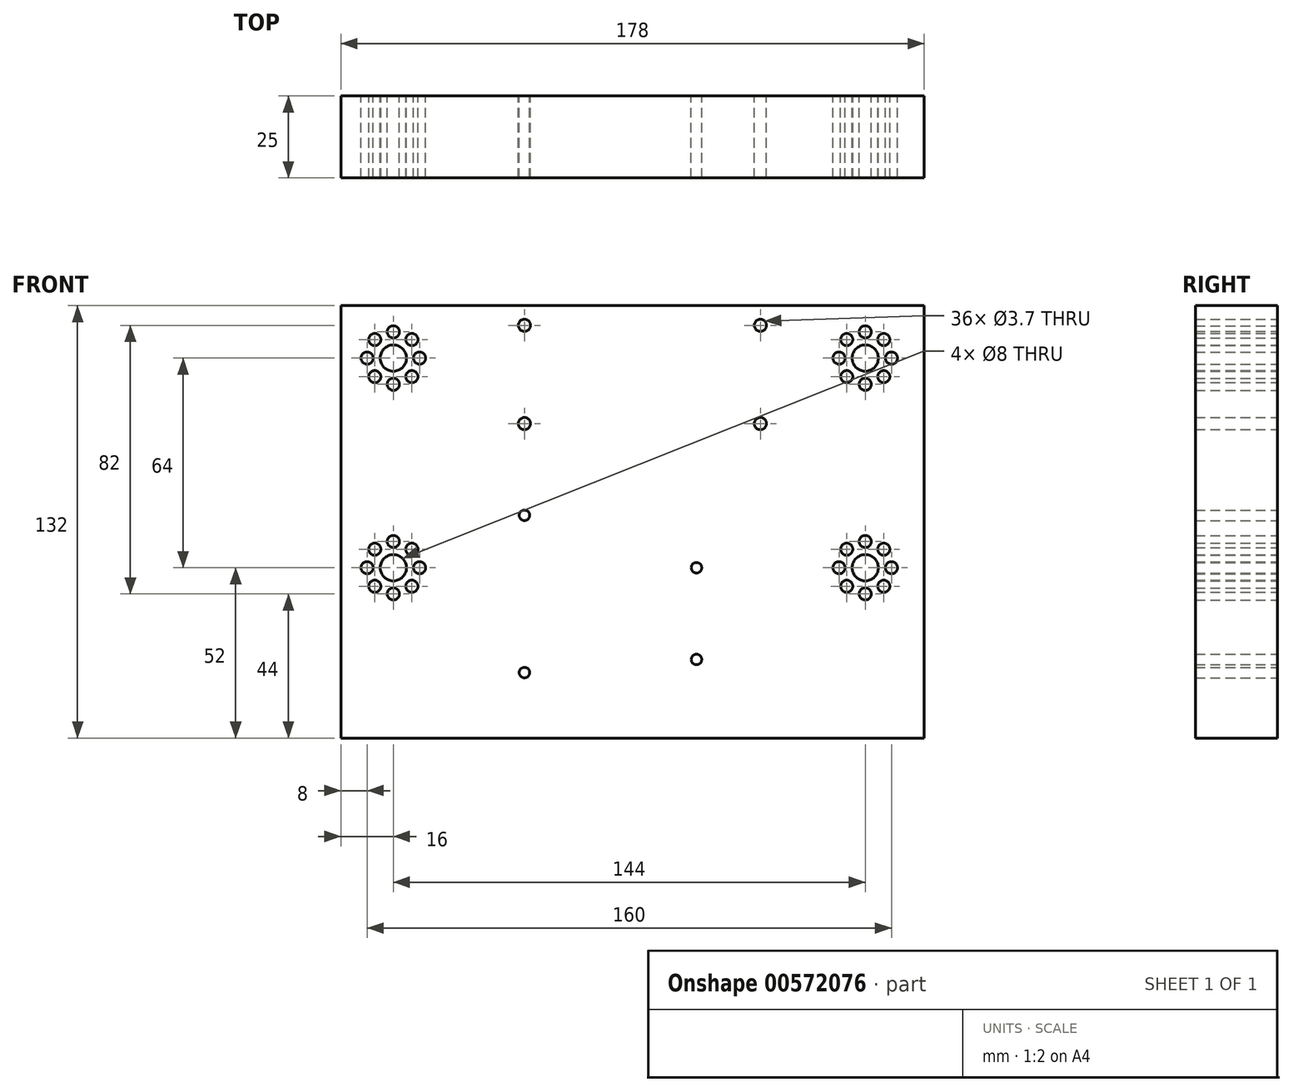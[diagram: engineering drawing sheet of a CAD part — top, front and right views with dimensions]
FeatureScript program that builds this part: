
annotation { "Feature Type Name" : "Feature", "Feature Type Description" : "" }
export const myFeature = defineFeature(function(context is Context, id is Id, definition is map)
    precondition{}
    {
        {
            var Q0;
            Q0=qCreatedBy(makeId("Front.planeOp"),FACE);
            var sketch = newSketch(context, id + "F0", { "sketchPlane" : qUnion([Q0])});
            skLineSegment(sketch, "E0.bottom", {"start": v(-89, 0) * mm, "end": v(89, 0) * mm});
            skLineSegment(sketch, "E0.top", {"start": v(-89, -132) * mm, "end": v(89, -132) * mm});
            skLineSegment(sketch, "E0.left", {"start": v(-89, 0) * mm, "end": v(-89, -132) * mm});
            skLineSegment(sketch, "E0.right", {"start": v(89, 0) * mm, "end": v(89, -132) * mm});
            skCircle(sketch, "E1", {"center": v(-73, -16) * mm, "radius": 4 * mm});
            skCircle(sketch, "E2", {"center": v(-73, -24) * mm, "radius": 1.85 * mm});
            skCircle(sketch, "E3.1.0", {"center": v(-67.34, -21.66) * mm, "radius": 1.85 * mm});
            skCircle(sketch, "E3.2.0", {"center": v(-65, -16) * mm, "radius": 1.85 * mm});
            skCircle(sketch, "E3.3.0", {"center": v(-67.34, -10.34) * mm, "radius": 1.85 * mm});
            skCircle(sketch, "E3.4.0", {"center": v(-73, -8) * mm, "radius": 1.85 * mm});
            skCircle(sketch, "E3.5.0", {"center": v(-78.66, -10.34) * mm, "radius": 1.85 * mm});
            skCircle(sketch, "E3.6.0", {"center": v(-81, -16) * mm, "radius": 1.85 * mm});
            skCircle(sketch, "E3.7.0", {"center": v(-78.66, -21.66) * mm, "radius": 1.85 * mm});
            skCircle(sketch, "E4.0.1.0", {"center": v(-73, -80) * mm, "radius": 4 * mm});
            skPoint(sketch, "E4.0.1.1", {"position": v(-73, -80) * mm});
            skCircle(sketch, "E4.0.1.2", {"center": v(-73, -88) * mm, "radius": 1.85 * mm});
            skCircle(sketch, "E4.0.1.3", {"center": v(-67.34, -85.66) * mm, "radius": 1.85 * mm});
            skCircle(sketch, "E4.0.1.4", {"center": v(-65, -80) * mm, "radius": 1.85 * mm});
            skCircle(sketch, "E4.0.1.5", {"center": v(-67.34, -74.34) * mm, "radius": 1.85 * mm});
            skCircle(sketch, "E4.0.1.6", {"center": v(-78.66, -74.34) * mm, "radius": 1.85 * mm});
            skCircle(sketch, "E4.0.1.7", {"center": v(-73, -72) * mm, "radius": 1.85 * mm});
            skCircle(sketch, "E4.0.1.8", {"center": v(-81, -80) * mm, "radius": 1.85 * mm});
            skCircle(sketch, "E4.0.1.9", {"center": v(-78.66, -85.66) * mm, "radius": 1.85 * mm});
            skCircle(sketch, "E4.1.0.0", {"center": v(71, -16) * mm, "radius": 4 * mm});
            skPoint(sketch, "E4.1.0.1", {"position": v(71, -16) * mm});
            skCircle(sketch, "E4.1.0.2", {"center": v(71, -24) * mm, "radius": 1.85 * mm});
            skCircle(sketch, "E4.1.0.3", {"center": v(76.66, -21.66) * mm, "radius": 1.85 * mm});
            skCircle(sketch, "E4.1.0.4", {"center": v(79, -16) * mm, "radius": 1.85 * mm});
            skCircle(sketch, "E4.1.0.5", {"center": v(76.66, -10.34) * mm, "radius": 1.85 * mm});
            skCircle(sketch, "E4.1.0.6", {"center": v(65.34, -10.34) * mm, "radius": 1.85 * mm});
            skCircle(sketch, "E4.1.0.7", {"center": v(71, -8) * mm, "radius": 1.85 * mm});
            skCircle(sketch, "E4.1.0.8", {"center": v(63, -16) * mm, "radius": 1.85 * mm});
            skCircle(sketch, "E4.1.0.9", {"center": v(65.34, -21.66) * mm, "radius": 1.85 * mm});
            skCircle(sketch, "E4.1.1.0", {"center": v(71, -80) * mm, "radius": 4 * mm});
            skPoint(sketch, "E4.1.1.1", {"position": v(71, -80) * mm});
            skCircle(sketch, "E4.1.1.2", {"center": v(71, -88) * mm, "radius": 1.85 * mm});
            skCircle(sketch, "E4.1.1.3", {"center": v(76.66, -85.66) * mm, "radius": 1.85 * mm});
            skCircle(sketch, "E4.1.1.4", {"center": v(79, -80) * mm, "radius": 1.85 * mm});
            skCircle(sketch, "E4.1.1.5", {"center": v(76.66, -74.34) * mm, "radius": 1.85 * mm});
            skCircle(sketch, "E4.1.1.6", {"center": v(65.34, -74.34) * mm, "radius": 1.85 * mm});
            skCircle(sketch, "E4.1.1.7", {"center": v(71, -72) * mm, "radius": 1.85 * mm});
            skCircle(sketch, "E4.1.1.8", {"center": v(63, -80) * mm, "radius": 1.85 * mm});
            skCircle(sketch, "E4.1.1.9", {"center": v(65.34, -85.66) * mm, "radius": 1.85 * mm});
            skLineSegment(sketch, "E4.direction1", {"start": v(-78.66, -21.66) * mm, "end": v(65.34, -21.66) * mm, "construction": true});
            skLineSegment(sketch, "E4.direction2", {"start": v(-78.66, -21.66) * mm, "end": v(-78.66, -85.66) * mm, "construction": true});
            skCircle(sketch, "E5", {"center": v(-33, -6) * mm, "radius": 1.85 * mm});
            skCircle(sketch, "E6", {"center": v(39, -6) * mm, "radius": 1.85 * mm});
            skCircle(sketch, "E7", {"center": v(39, -36) * mm, "radius": 1.85 * mm});
            skCircle(sketch, "E8", {"center": v(-33, -36) * mm, "radius": 1.85 * mm});
            skLineSegment(sketch, "E9.direction1", {"start": v(-81.6, -11.8) * mm, "end": v(62.4, -11.8) * mm, "construction": true});
            skCircle(sketch, "E10", {"center": v(-33, -64) * mm, "radius": 1.6 * mm});
            skCircle(sketch, "E11", {"center": v(19.5, -80) * mm, "radius": 1.6 * mm});
            skCircle(sketch, "E12", {"center": v(19.5, -108) * mm, "radius": 1.6 * mm});
            skCircle(sketch, "E13", {"center": v(-33, -112) * mm, "radius": 1.6 * mm});
            skSolve(sketch);
        }
        {
            var Q0;
            Q0 = qSketchRegion(id + "F0", true);
            extrude(context, id + "F1", {"entities" : qUnion([Q0]), "depth" : 25 * mm, "offsetDistance" : 25 * mm});
        }
    });
